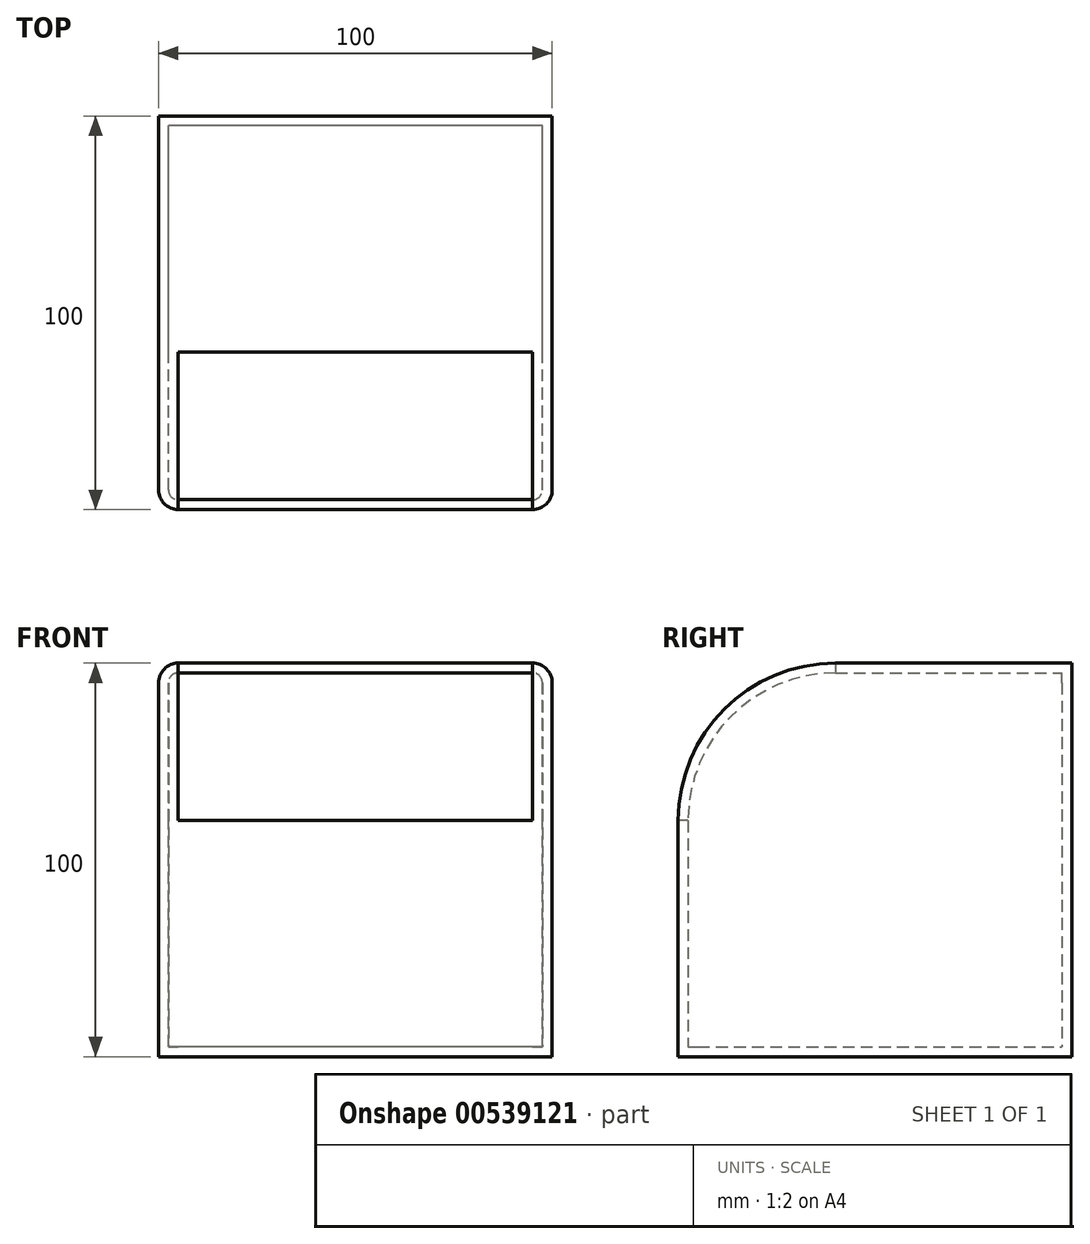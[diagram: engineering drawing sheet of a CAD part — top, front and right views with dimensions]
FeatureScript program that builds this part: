
annotation { "Feature Type Name" : "Feature", "Feature Type Description" : "" }
export const myFeature = defineFeature(function(context is Context, id is Id, definition is map)
    precondition{}
    {
        {
            var Q0;
            Q0=qCreatedBy(makeId("Top.planeOp"),FACE);
            var sketch = newSketch(context, id + "F0", { "sketchPlane" : qUnion([Q0])});
            skLineSegment(sketch, "E0.bottom", {"start": v(50, -50) * mm, "end": v(-50, -50) * mm});
            skLineSegment(sketch, "E0.top", {"start": v(50, 50) * mm, "end": v(-50, 50) * mm});
            skLineSegment(sketch, "E0.left", {"start": v(50, -50) * mm, "end": v(50, 50) * mm});
            skLineSegment(sketch, "E0.right", {"start": v(-50, -50) * mm, "end": v(-50, 50) * mm});
            skPoint(sketch, "E0.middle", {"position": v(0, 0) * mm});
            skSolve(sketch);
        }
        {
            var Q0;
            Q0=makeQuery(id+"F0.imprint","IMPRINT",FACE,{"disambiguationData":[TD([[makeQuery(id+"F0.imprint","IMPRINT",EDGE,{"derivedFrom":sQuery(id+"F0.wireOp",EDGE,"E0.bottom")}),-1.0]])]});
            extrude(context, id + "F1", {"entities" : qUnion([Q0]), "depth" : 100 * mm, "offsetDistance" : 25 * mm});
        }
        {
            var Q0;
            Q0=makeQuery(id+"F1.opExtrude","CAP_EDGE",EDGE,{"disambiguationData":[OSD([sQuery(id+"F0.wireOp",EDGE,"E0.bottom")])],"isStart":false});
            fillet(context, id + "F2", {"entities" : qUnion([Q0]), "radius" : 40 * mm, "tangentPropagation" : true, "allowEdgeOverflow" : false});
        }
        {
            var Q0;
            Q0=makeQuery(id+"F1.opExtrude","CAP_EDGE",EDGE,{"disambiguationData":[OSD([sQuery(id+"F0.wireOp",EDGE,"E0.left")])],"isStart":false});
            var Q1;
            Q1=makeQuery(id+"F1.opExtrude","CAP_EDGE",EDGE,{"disambiguationData":[OSD([sQuery(id+"F0.wireOp",EDGE,"E0.right")])],"isStart":false});
            fillet(context, id + "F3", {"entities" : qUnion([Q0, Q1]), "radius" : 5 * mm, "tangentPropagation" : true, "allowEdgeOverflow" : false});
        }
        {
            var Q0;
            Q0=makeQuery(id+"F2.opFillet","BLEND_FACE",FACE,{"disambiguationData":[OSD([sQuery(id+"F0.wireOp",EDGE,"E0.bottom")])]});
            shell(context, id + "F4", {"entities" : qUnion([Q0]), "thickness" : 2.5 * mm});
        }
    });
